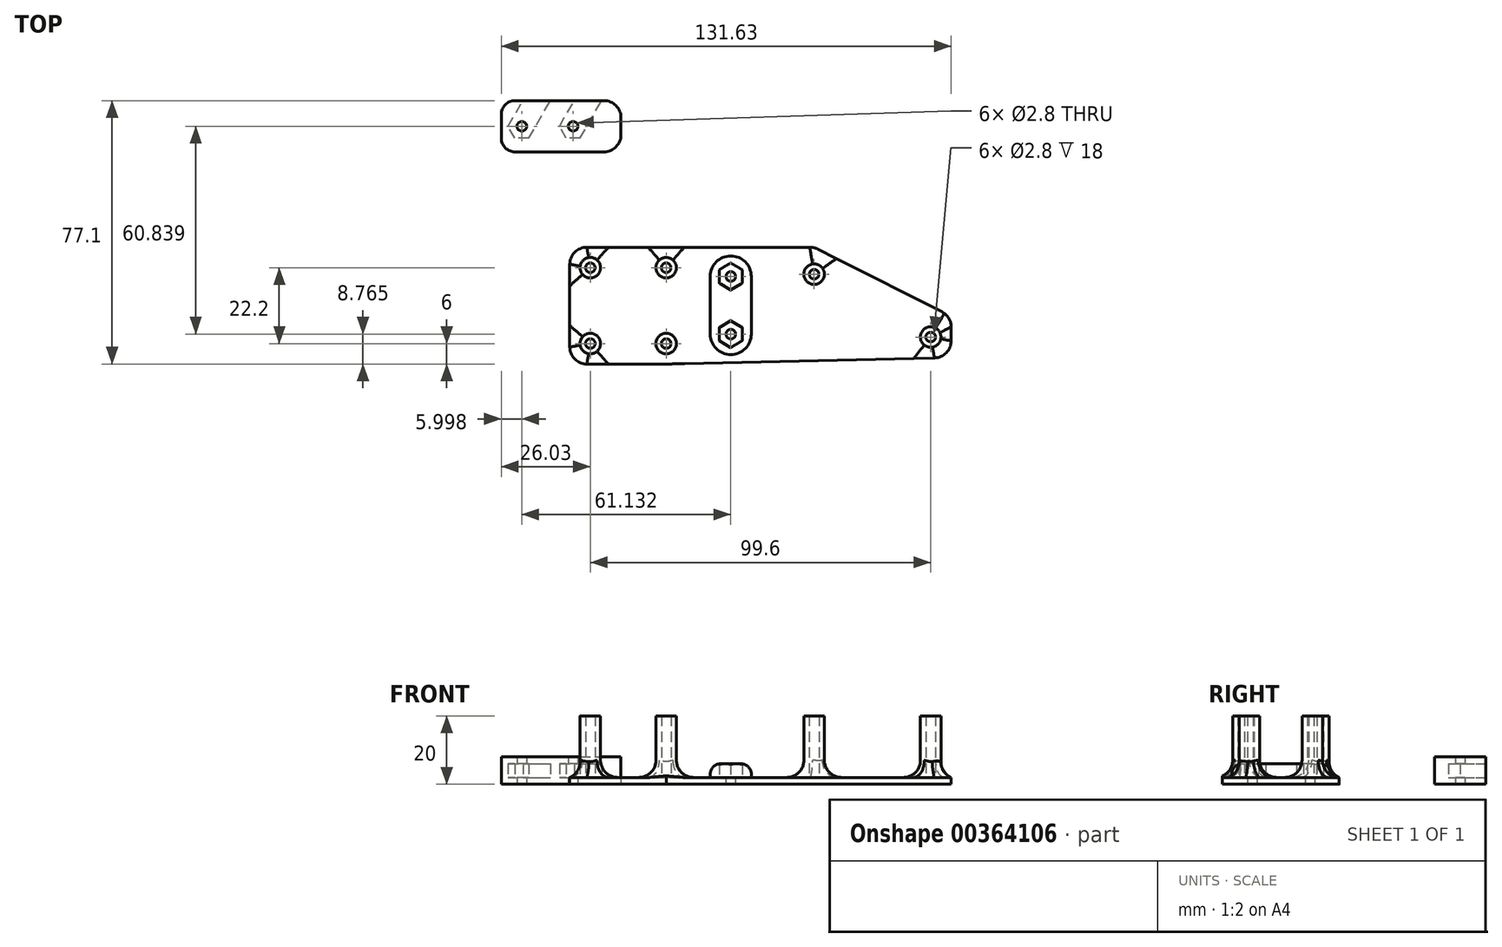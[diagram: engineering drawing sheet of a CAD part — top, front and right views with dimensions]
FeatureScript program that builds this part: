
annotation { "Feature Type Name" : "Feature", "Feature Type Description" : "" }
export const myFeature = defineFeature(function(context is Context, id is Id, definition is map)
    precondition{}
    {
        {
            var Q0;
            Q0=qCreatedBy(makeId("Top.planeOp"),FACE);
            var sketch = newSketch(context, id + "F0", { "sketchPlane" : qUnion([Q0])});
            skLineSegment(sketch, "E0.bottom", {"start": v(-26.1, 11.1) * mm, "end": v(-3.9, 11.1) * mm, "construction": true});
            skLineSegment(sketch, "E0.top", {"start": v(-26.1, -11.1) * mm, "end": v(-3.9, -11.1) * mm, "construction": true});
            skLineSegment(sketch, "E0.left", {"start": v(-26.1, 11.1) * mm, "end": v(-26.1, -11.1) * mm, "construction": true});
            skLineSegment(sketch, "E0.right", {"start": v(-3.9, 11.1) * mm, "end": v(-3.9, -11.1) * mm, "construction": true});
            skCircle(sketch, "E1", {"center": v(-26.1, 11.1) * mm, "radius": 1.4 * mm});
            skCircle(sketch, "E2", {"center": v(-3.9, 11.1) * mm, "radius": 1.4 * mm});
            skCircle(sketch, "E3", {"center": v(-3.9, -11.1) * mm, "radius": 1.4 * mm});
            skCircle(sketch, "E4", {"center": v(-26.1, -11.1) * mm, "radius": 1.4 * mm});
            skCircle(sketch, "E5", {"center": v(-26.1, 11.1) * mm, "radius": 3 * mm});
            skCircle(sketch, "E6", {"center": v(-3.9, 11.1) * mm, "radius": 3 * mm});
            skCircle(sketch, "E7", {"center": v(-3.9, -11.1) * mm, "radius": 3 * mm});
            skCircle(sketch, "E8", {"center": v(-26.1, -11.1) * mm, "radius": 3 * mm});
            skLineSegment(sketch, "E9", {"start": v(-26.1, 11.1) * mm, "end": v(-3.9, -11.1) * mm, "construction": true});
            skLineSegment(sketch, "E10", {"start": v(-26.1, -11.1) * mm, "end": v(-3.9, 11.1) * mm, "construction": true});
            skPoint(sketch, "E11", {"position": v(-15, 0) * mm});
            skLineSegment(sketch, "E12.bottom", {"start": v(-30, 15) * mm, "end": v(0, 15) * mm, "construction": true});
            skLineSegment(sketch, "E12.top", {"start": v(-30, -15) * mm, "end": v(0, -15) * mm, "construction": true});
            skLineSegment(sketch, "E12.left", {"start": v(-30, 15) * mm, "end": v(-30, -15) * mm, "construction": true});
            skLineSegment(sketch, "E12.right", {"start": v(0, 15) * mm, "end": v(0, -15) * mm, "construction": true});
            skLineSegment(sketch, "E13", {"start": v(-15, 15) * mm, "end": v(-15, -15) * mm, "construction": true});
            skLineSegment(sketch, "E14", {"start": v(-30, 0) * mm, "end": v(0, 0) * mm, "construction": true});
            skLineSegment(sketch, "E15.bottom", {"start": v(30, -12) * mm, "end": v(84, -12) * mm, "construction": true});
            skLineSegment(sketch, "E15.top", {"start": v(30, 12) * mm, "end": v(84, 12) * mm, "construction": true});
            skLineSegment(sketch, "E15.left", {"start": v(30, -12) * mm, "end": v(30, 12) * mm, "construction": true});
            skLineSegment(sketch, "E15.right", {"start": v(84, -12) * mm, "end": v(84, 12) * mm, "construction": true});
            skCircle(sketch, "E16", {"center": v(39.4, 9.2) * mm, "radius": 1.4 * mm});
            skCircle(sketch, "E17", {"center": v(73.5, -9.2) * mm, "radius": 1.4 * mm});
            skLineSegment(sketch, "E18", {"start": v(0, 0) * mm, "end": v(15, 0) * mm, "construction": true});
            skCircle(sketch, "E19", {"center": v(39.4, 9.2) * mm, "radius": 3 * mm});
            skCircle(sketch, "E20", {"center": v(73.5, -9.2) * mm, "radius": 3 * mm});
            skLineSegment(sketch, "E21.bottom", {"start": v(-32.1, 17.1) * mm, "end": v(79.5, 17.1) * mm});
            skLineSegment(sketch, "E21.top", {"start": v(-32.1, -17.1) * mm, "end": v(79.5, -17.1) * mm});
            skLineSegment(sketch, "E21.left", {"start": v(-32.1, 17.1) * mm, "end": v(-32.1, -17.1) * mm});
            skLineSegment(sketch, "E21.right", {"start": v(79.5, 17.1) * mm, "end": v(79.5, -3.2) * mm, "construction": true});
            skLineSegment(sketch, "E22", {"start": v(-3.9, -17.1) * mm, "end": v(79.5, -15.2) * mm});
            skLineSegment(sketch, "E23", {"start": v(73.5, -12.2) * mm, "end": v(79.5, -12.2) * mm, "construction": true});
            skLineSegment(sketch, "E24", {"start": v(73.5, -6.2) * mm, "end": v(79.5, -6.2) * mm, "construction": true});
            skLineSegment(sketch, "E25", {"start": v(39.4, 17.1) * mm, "end": v(79.5, -3.2) * mm});
            skLineSegment(sketch, "E26", {"start": v(79.5, -3.2) * mm, "end": v(79.5, -15.2) * mm});
            skLineSegment(sketch, "E27", {"start": v(79.5, -15.2) * mm, "end": v(79.5, -17.1) * mm, "construction": true});
            skLineSegment(sketch, "E28", {"start": v(15, 17.1) * mm, "end": v(15, 0) * mm, "construction": true});
            skPoint(sketch, "E28.startSnap0", {"position": v(15, 0) * mm});
            skLineSegment(sketch, "E29", {"start": v(15, 0) * mm, "end": v(30, 0) * mm, "construction": true});
            skLineSegment(sketch, "E30", {"start": v(15, 0) * mm, "end": v(15, -16.67) * mm, "construction": true});
            skCircle(sketch, "E31.cCircle", {"center": v(15, -8.33) * mm, "radius": 3.9 * mm, "construction": true});
            skLineSegment(sketch, "E31.0", {"start": v(11.62, -6.38) * mm, "end": v(15, -4.43) * mm});
            skLineSegment(sketch, "E31.1", {"start": v(15, -4.43) * mm, "end": v(18.38, -6.38) * mm});
            skLineSegment(sketch, "E31.2", {"start": v(18.38, -6.38) * mm, "end": v(18.38, -10.28) * mm});
            skLineSegment(sketch, "E31.3", {"start": v(18.38, -10.28) * mm, "end": v(15, -12.23) * mm});
            skLineSegment(sketch, "E31.4", {"start": v(15, -12.23) * mm, "end": v(11.62, -10.28) * mm});
            skLineSegment(sketch, "E31.5", {"start": v(11.62, -10.28) * mm, "end": v(11.62, -6.38) * mm});
            skCircle(sketch, "E32.cCircle", {"center": v(15, 8.55) * mm, "radius": 3.9 * mm, "construction": true});
            skLineSegment(sketch, "E32.0", {"start": v(18.38, 6.6) * mm, "end": v(15, 4.65) * mm});
            skLineSegment(sketch, "E32.1", {"start": v(15, 4.65) * mm, "end": v(11.62, 6.6) * mm});
            skLineSegment(sketch, "E32.2", {"start": v(11.62, 6.6) * mm, "end": v(11.62, 10.5) * mm});
            skLineSegment(sketch, "E32.3", {"start": v(11.62, 10.5) * mm, "end": v(15, 12.45) * mm});
            skLineSegment(sketch, "E32.4", {"start": v(15, 12.45) * mm, "end": v(18.38, 10.5) * mm});
            skLineSegment(sketch, "E32.5", {"start": v(18.38, 10.5) * mm, "end": v(18.38, 6.6) * mm});
            skCircle(sketch, "E33", {"center": v(15, -8.33) * mm, "radius": 6 * mm});
            skCircle(sketch, "E34", {"center": v(15, 8.55) * mm, "radius": 6 * mm});
            skLineSegment(sketch, "E35", {"start": v(9, -8.33) * mm, "end": v(9, 8.55) * mm});
            skPoint(sketch, "E35.startSnap0", {"position": v(11.62, -8.33) * mm});
            skLineSegment(sketch, "E36", {"start": v(21, -8.33) * mm, "end": v(21, 8.55) * mm});
            skPoint(sketch, "E36.startSnap0", {"position": v(18.38, -8.33) * mm});
            skCircle(sketch, "E37", {"center": v(15, 8.55) * mm, "radius": 1.4 * mm});
            skCircle(sketch, "E38", {"center": v(15, -8.33) * mm, "radius": 1.4 * mm});
            skSolve(sketch);
        }
        {
            var Q0;
            Q0=makeQuery(id+"F0.imprint","IMPRINT",FACE,{"disambiguationData":[TD([[makeQuery(id+"F0.imprint","IMPRINT",EDGE,{"derivedFrom":sQuery(id+"F0.wireOp",EDGE,"E5")}),-1.0]])]});
            var Q1;
            Q1=makeQuery(id+"F0.imprint","IMPRINT",FACE,{"disambiguationData":[TD([[makeQuery(id+"F0.imprint","IMPRINT",EDGE,{"derivedFrom":sQuery(id+"F0.wireOp",EDGE,"E3")}),-1.0]])]});
            var Q2;
            Q2=makeQuery(id+"F0.imprint","IMPRINT",FACE,{"disambiguationData":[TD([[makeQuery(id+"F0.imprint","IMPRINT",EDGE,{"derivedFrom":sQuery(id+"F0.wireOp",EDGE,"E4")}),-1.0]])]});
            var Q3;
            Q3=makeQuery(id+"F0.imprint","IMPRINT",FACE,{"disambiguationData":[TD([[makeQuery(id+"F0.imprint","IMPRINT",EDGE,{"derivedFrom":sQuery(id+"F0.wireOp",EDGE,"E4")}),1.0]])]});
            var Q4;
            Q4=makeQuery(id+"F0.imprint","IMPRINT",FACE,{"disambiguationData":[TD([[makeQuery(id+"F0.imprint","IMPRINT",EDGE,{"derivedFrom":sQuery(id+"F0.wireOp",EDGE,"E3")}),1.0]])]});
            var Q5;
            Q5=makeQuery(id+"F0.imprint","IMPRINT",FACE,{"disambiguationData":[TD([[makeQuery(id+"F0.imprint","IMPRINT",EDGE,{"derivedFrom":sQuery(id+"F0.wireOp",EDGE,"E2")}),-1.0]])]});
            var Q6;
            Q6=makeQuery(id+"F0.imprint","IMPRINT",FACE,{"disambiguationData":[TD([[makeQuery(id+"F0.imprint","IMPRINT",EDGE,{"derivedFrom":sQuery(id+"F0.wireOp",EDGE,"E2")}),1.0]])]});
            var Q7;
            Q7=makeQuery(id+"F0.imprint","IMPRINT",FACE,{"disambiguationData":[TD([[makeQuery(id+"F0.imprint","IMPRINT",EDGE,{"derivedFrom":sQuery(id+"F0.wireOp",EDGE,"E1")}),1.0]])]});
            var Q8;
            Q8=makeQuery(id+"F0.imprint","IMPRINT",FACE,{"disambiguationData":[TD([[makeQuery(id+"F0.imprint","IMPRINT",EDGE,{"derivedFrom":sQuery(id+"F0.wireOp",EDGE,"E1")}),-1.0]])]});
            var Q9;
            Q9=makeQuery(id+"F0.imprint","IMPRINT",FACE,{"disambiguationData":[TD([[makeQuery(id+"F0.imprint","IMPRINT",EDGE,{"derivedFrom":sQuery(id+"F0.wireOp",EDGE,"E16")}),-1.0]])]});
            var Q10;
            Q10=makeQuery(id+"F0.imprint","IMPRINT",FACE,{"disambiguationData":[TD([[makeQuery(id+"F0.imprint","IMPRINT",EDGE,{"derivedFrom":sQuery(id+"F0.wireOp",EDGE,"E16")}),1.0]])]});
            var Q11;
            {var subQ0=sQuery(id+"F0.wireOp",EDGE,"E35");Q11=makeQuery(id+"F0.imprint","IMPRINT",FACE,{"disambiguationData":[TD([[makeQuery(id+"F0.imprint","IMPRINT",EDGE,{"derivedFrom":subQ0}),-1.0]])]});}
            var Q12;
            Q12=makeQuery(id+"F0.imprint","IMPRINT",FACE,{"disambiguationData":[TD([[makeQuery(id+"F0.imprint","IMPRINT",EDGE,{"derivedFrom":sQuery(id+"F0.wireOp",EDGE,"E32.0")}),1.0]])]});
            var Q13;
            Q13=makeQuery(id+"F0.imprint","IMPRINT",FACE,{"disambiguationData":[TD([[makeQuery(id+"F0.imprint","IMPRINT",EDGE,{"derivedFrom":sQuery(id+"F0.wireOp",EDGE,"E32.0")}),-1.0]])]});
            var Q14;
            Q14=makeQuery(id+"F0.imprint","IMPRINT",FACE,{"disambiguationData":[TD([[makeQuery(id+"F0.imprint","IMPRINT",EDGE,{"derivedFrom":sQuery(id+"F0.wireOp",EDGE,"E31.0")}),-1.0]])]});
            var Q15;
            Q15=makeQuery(id+"F0.imprint","IMPRINT",FACE,{"disambiguationData":[TD([[makeQuery(id+"F0.imprint","IMPRINT",EDGE,{"derivedFrom":sQuery(id+"F0.wireOp",EDGE,"E31.0")}),1.0]])]});
            var Q16;
            Q16=makeQuery(id+"F0.imprint","IMPRINT",FACE,{"disambiguationData":[TD([[makeQuery(id+"F0.imprint","IMPRINT",EDGE,{"derivedFrom":sQuery(id+"F0.wireOp",EDGE,"E17")}),-1.0]])]});
            var Q17;
            Q17=makeQuery(id+"F0.imprint","IMPRINT",FACE,{"disambiguationData":[TD([[makeQuery(id+"F0.imprint","IMPRINT",EDGE,{"derivedFrom":sQuery(id+"F0.wireOp",EDGE,"E17")}),1.0]])]});
            extrude(context, id + "F1", {"entities" : qUnion([Q0, Q1, Q2, Q3, Q4, Q5, Q6, Q7, Q8, Q9, Q10, Q11, Q12, Q13, Q14, Q15, Q16, Q17]), "depth" : 2 * mm});
        }
        {
            var Q0;
            Q0=makeQuery(id+"F0.imprint","IMPRINT",FACE,{"disambiguationData":[TD([[makeQuery(id+"F0.imprint","IMPRINT",EDGE,{"derivedFrom":sQuery(id+"F0.wireOp",EDGE,"E4")}),-1.0]])]});
            var Q1;
            Q1=makeQuery(id+"F0.imprint","IMPRINT",FACE,{"disambiguationData":[TD([[makeQuery(id+"F0.imprint","IMPRINT",EDGE,{"derivedFrom":sQuery(id+"F0.wireOp",EDGE,"E3")}),-1.0]])]});
            var Q2;
            Q2=makeQuery(id+"F0.imprint","IMPRINT",FACE,{"disambiguationData":[TD([[makeQuery(id+"F0.imprint","IMPRINT",EDGE,{"derivedFrom":sQuery(id+"F0.wireOp",EDGE,"E2")}),-1.0]])]});
            var Q3;
            Q3=makeQuery(id+"F0.imprint","IMPRINT",FACE,{"disambiguationData":[TD([[makeQuery(id+"F0.imprint","IMPRINT",EDGE,{"derivedFrom":sQuery(id+"F0.wireOp",EDGE,"E1")}),-1.0]])]});
            var Q4;
            Q4=makeQuery(id+"F0.imprint","IMPRINT",FACE,{"disambiguationData":[TD([[makeQuery(id+"F0.imprint","IMPRINT",EDGE,{"derivedFrom":sQuery(id+"F0.wireOp",EDGE,"E16")}),-1.0]])]});
            var Q5;
            Q5=makeQuery(id+"F0.imprint","IMPRINT",FACE,{"disambiguationData":[TD([[makeQuery(id+"F0.imprint","IMPRINT",EDGE,{"derivedFrom":sQuery(id+"F0.wireOp",EDGE,"E17")}),-1.0]])]});
            extrude(context, id + "F2", {"entities" : qUnion([Q0, Q1, Q2, Q3, Q4, Q5]), "operationType" : NewBodyOperationType.ADD, "depth" : 20 * mm});
        }
        {
            var Q0;
            Q0=makeQuery(id+"F0.imprint","IMPRINT",FACE,{"disambiguationData":[TD([[makeQuery(id+"F0.imprint","IMPRINT",EDGE,{"derivedFrom":sQuery(id+"F0.wireOp",EDGE,"E31.0")}),1.0]])]});
            var Q1;
            Q1=makeQuery(id+"F0.imprint","IMPRINT",FACE,{"disambiguationData":[TD([[makeQuery(id+"F0.imprint","IMPRINT",EDGE,{"derivedFrom":sQuery(id+"F0.wireOp",EDGE,"E32.0")}),1.0]])]});
            var Q2;
            {var subQ0=sQuery(id+"F0.wireOp",EDGE,"E35");Q2=makeQuery(id+"F0.imprint","IMPRINT",FACE,{"disambiguationData":[TD([[makeQuery(id+"F0.imprint","IMPRINT",EDGE,{"derivedFrom":subQ0}),-1.0]])]});}
            extrude(context, id + "F3", {"entities" : qUnion([Q0, Q1, Q2]), "operationType" : NewBodyOperationType.ADD, "depth" : 6 * mm});
        }
        {
            var Q0;
            Q0=makeQuery(id+"F1.opExtrude","SWEPT_EDGE",EDGE,{"disambiguationData":[OSD([sQuery(id+"F0.wireOp",EDGE,"E21.top"),sQuery(id+"F0.wireOp",EDGE,"E21.left")])]});
            var Q1;
            Q1=makeQuery(id+"F1.opExtrude","SWEPT_EDGE",EDGE,{"disambiguationData":[OSD([sQuery(id+"F0.wireOp",EDGE,"E21.bottom"),sQuery(id+"F0.wireOp",EDGE,"E21.left")])]});
            var Q2;
            Q2=makeQuery(id+"F1.opExtrude","SWEPT_EDGE",EDGE,{"disambiguationData":[OSD([sQuery(id+"F0.wireOp",EDGE,"E21.bottom"),sQuery(id+"F0.wireOp",EDGE,"E25")])]});
            var Q3;
            Q3=makeQuery(id+"F1.opExtrude","SWEPT_EDGE",EDGE,{"disambiguationData":[OSD([sQuery(id+"F0.wireOp",EDGE,"E25"),sQuery(id+"F0.wireOp",EDGE,"E26")])]});
            var Q4;
            Q4=makeQuery(id+"F1.opExtrude","SWEPT_EDGE",EDGE,{"disambiguationData":[OSD([sQuery(id+"F0.wireOp",EDGE,"E22"),sQuery(id+"F0.wireOp",EDGE,"E26")])]});
            fillet(context, id + "F4", {"entities" : qUnion([Q0, Q1, Q2, Q3, Q4]), "radius" : 5 * mm, "tangentPropagation" : true, "allowEdgeOverflow" : false});
        }
        {
            var Q0;
            Q0=makeQuery(id+"F2.boolean.opBoolean","INTERSECT",EDGE,{"derivedFrom":[makeQuery(id+"F1.opExtrude","CAP_FACE",FACE,{"disambiguationData":[OSD([sQuery(id+"F0.wireOp",EDGE,"E21.bottom"),sQuery(id+"F0.wireOp",EDGE,"E21.top"),sQuery(id+"F0.wireOp",EDGE,"E21.left"),sQuery(id+"F0.wireOp",EDGE,"E22"),sQuery(id+"F0.wireOp",EDGE,"E25"),sQuery(id+"F0.wireOp",EDGE,"E26"),sQuery(id+"F0.wireOp",EDGE,"E37"),sQuery(id+"F0.wireOp",EDGE,"E38")])],"isStart":false}),makeQuery(id+"F2.opExtrude","SWEPT_FACE",FACE,{"disambiguationData":[OSD([sQuery(id+"F0.wireOp",EDGE,"E5")])]})]});
            var Q1;
            Q1=makeQuery(id+"F2.boolean.opBoolean","INTERSECT",EDGE,{"derivedFrom":[makeQuery(id+"F1.opExtrude","CAP_FACE",FACE,{"disambiguationData":[OSD([sQuery(id+"F0.wireOp",EDGE,"E21.bottom"),sQuery(id+"F0.wireOp",EDGE,"E21.top"),sQuery(id+"F0.wireOp",EDGE,"E21.left"),sQuery(id+"F0.wireOp",EDGE,"E22"),sQuery(id+"F0.wireOp",EDGE,"E25"),sQuery(id+"F0.wireOp",EDGE,"E26"),sQuery(id+"F0.wireOp",EDGE,"E37"),sQuery(id+"F0.wireOp",EDGE,"E38")])],"isStart":false}),makeQuery(id+"F2.opExtrude","SWEPT_FACE",FACE,{"disambiguationData":[OSD([sQuery(id+"F0.wireOp",EDGE,"E6")])]})]});
            var Q2;
            Q2=makeQuery(id+"F2.boolean.opBoolean","INTERSECT",EDGE,{"derivedFrom":[makeQuery(id+"F1.opExtrude","CAP_FACE",FACE,{"disambiguationData":[OSD([sQuery(id+"F0.wireOp",EDGE,"E21.bottom"),sQuery(id+"F0.wireOp",EDGE,"E21.top"),sQuery(id+"F0.wireOp",EDGE,"E21.left"),sQuery(id+"F0.wireOp",EDGE,"E22"),sQuery(id+"F0.wireOp",EDGE,"E25"),sQuery(id+"F0.wireOp",EDGE,"E26"),sQuery(id+"F0.wireOp",EDGE,"E37"),sQuery(id+"F0.wireOp",EDGE,"E38")])],"isStart":false}),makeQuery(id+"F2.opExtrude","SWEPT_FACE",FACE,{"disambiguationData":[OSD([sQuery(id+"F0.wireOp",EDGE,"E8")])]})]});
            var Q3;
            Q3=makeQuery(id+"F2.boolean.opBoolean","INTERSECT",EDGE,{"derivedFrom":[makeQuery(id+"F1.opExtrude","CAP_FACE",FACE,{"disambiguationData":[OSD([sQuery(id+"F0.wireOp",EDGE,"E21.bottom"),sQuery(id+"F0.wireOp",EDGE,"E21.top"),sQuery(id+"F0.wireOp",EDGE,"E21.left"),sQuery(id+"F0.wireOp",EDGE,"E22"),sQuery(id+"F0.wireOp",EDGE,"E25"),sQuery(id+"F0.wireOp",EDGE,"E26"),sQuery(id+"F0.wireOp",EDGE,"E37"),sQuery(id+"F0.wireOp",EDGE,"E38")])],"isStart":false}),makeQuery(id+"F2.opExtrude","SWEPT_FACE",FACE,{"disambiguationData":[OSD([sQuery(id+"F0.wireOp",EDGE,"E7")])]})]});
            var Q4;
            Q4=makeQuery(id+"F2.boolean.opBoolean","INTERSECT",EDGE,{"derivedFrom":[makeQuery(id+"F1.opExtrude","CAP_FACE",FACE,{"disambiguationData":[OSD([sQuery(id+"F0.wireOp",EDGE,"E21.bottom"),sQuery(id+"F0.wireOp",EDGE,"E21.top"),sQuery(id+"F0.wireOp",EDGE,"E21.left"),sQuery(id+"F0.wireOp",EDGE,"E22"),sQuery(id+"F0.wireOp",EDGE,"E25"),sQuery(id+"F0.wireOp",EDGE,"E26"),sQuery(id+"F0.wireOp",EDGE,"E37"),sQuery(id+"F0.wireOp",EDGE,"E38")])],"isStart":false}),makeQuery(id+"F2.opExtrude","SWEPT_FACE",FACE,{"disambiguationData":[OSD([sQuery(id+"F0.wireOp",EDGE,"E19")])]})]});
            var Q5;
            Q5=makeQuery(id+"F2.boolean.opBoolean","INTERSECT",EDGE,{"derivedFrom":[makeQuery(id+"F1.opExtrude","CAP_FACE",FACE,{"disambiguationData":[OSD([sQuery(id+"F0.wireOp",EDGE,"E21.bottom"),sQuery(id+"F0.wireOp",EDGE,"E21.top"),sQuery(id+"F0.wireOp",EDGE,"E21.left"),sQuery(id+"F0.wireOp",EDGE,"E22"),sQuery(id+"F0.wireOp",EDGE,"E25"),sQuery(id+"F0.wireOp",EDGE,"E26"),sQuery(id+"F0.wireOp",EDGE,"E37"),sQuery(id+"F0.wireOp",EDGE,"E38")])],"isStart":false}),makeQuery(id+"F2.opExtrude","SWEPT_FACE",FACE,{"disambiguationData":[OSD([sQuery(id+"F0.wireOp",EDGE,"E20")])]})]});
            fillet(context, id + "F5", {"entities" : qUnion([Q0, Q1, Q2, Q3, Q4, Q5]), "radius" : 5 * mm, "tangentPropagation" : true, "allowEdgeOverflow" : false});
        }
        {
            var Q0;
            Q0=makeQuery(id+"F3.opExtrude","CAP_EDGE",EDGE,{"disambiguationData":[OSD([sQuery(id+"F0.wireOp",EDGE,"E33")])],"isStart":false});
            fillet(context, id + "F6", {"entities" : qUnion([Q0]), "radius" : 3 * mm, "tangentPropagation" : true, "allowEdgeOverflow" : false});
        }
        {
            var Q0;
            Q0=qCreatedBy(makeId("Top.planeOp"),FACE);
            var sketch = newSketch(context, id + "F7", { "sketchPlane" : qUnion([Q0])});
            skLineSegment(sketch, "E39.bottom", {"start": v(-48.13, 60) * mm, "end": v(-45.8, 60) * mm});
            skLineSegment(sketch, "E39.top", {"start": v(-48.13, 45) * mm, "end": v(-22.13, 45) * mm});
            skLineSegment(sketch, "E39.left", {"start": v(-52.13, 56) * mm, "end": v(-52.13, 49) * mm});
            skLineSegment(sketch, "E39.right", {"start": v(-17.13, 55) * mm, "end": v(-17.13, 50) * mm});
            skCircle(sketch, "E40", {"center": v(-31.13, 52.5) * mm, "radius": 1.4 * mm});
            skCircle(sketch, "E41", {"center": v(-46.13, 52.5) * mm, "radius": 1.4 * mm});
            skLineSegment(sketch, "E42", {"start": v(-17.13, 52.5) * mm, "end": v(-52.13, 52.5) * mm, "construction": true});
            skCircle(sketch, "E43.cCircle", {"center": v(-31.13, 52.5) * mm, "radius": 4 * mm, "construction": true});
            skLineSegment(sketch, "E43.0", {"start": v(-27.13, 52.5) * mm, "end": v(-29.13, 49.04) * mm});
            skLineSegment(sketch, "E43.1", {"start": v(-29.13, 49.04) * mm, "end": v(-33.13, 49.04) * mm});
            skLineSegment(sketch, "E43.2", {"start": v(-33.13, 49.04) * mm, "end": v(-35.13, 52.5) * mm});
            skLineSegment(sketch, "E43.3", {"start": v(-35.13, 52.5) * mm, "end": v(-33.13, 55.97) * mm});
            skLineSegment(sketch, "E43.4", {"start": v(-33.13, 55.97) * mm, "end": v(-29.13, 55.97) * mm});
            skLineSegment(sketch, "E43.5", {"start": v(-29.13, 55.97) * mm, "end": v(-27.13, 52.5) * mm});
            skCircle(sketch, "E44.cCircle", {"center": v(-46.13, 52.5) * mm, "radius": 4 * mm, "construction": true});
            skLineSegment(sketch, "E44.0", {"start": v(-42.13, 52.5) * mm, "end": v(-44.13, 49.04) * mm});
            skLineSegment(sketch, "E44.1", {"start": v(-44.13, 49.04) * mm, "end": v(-48.13, 49.04) * mm});
            skLineSegment(sketch, "E44.2", {"start": v(-48.13, 49.04) * mm, "end": v(-50.13, 52.5) * mm});
            skLineSegment(sketch, "E44.3", {"start": v(-50.13, 52.5) * mm, "end": v(-48.13, 55.97) * mm});
            skLineSegment(sketch, "E44.4", {"start": v(-48.13, 55.97) * mm, "end": v(-44.13, 55.97) * mm});
            skLineSegment(sketch, "E44.5", {"start": v(-44.13, 55.97) * mm, "end": v(-42.13, 52.5) * mm});
            skLineSegment(sketch, "E45", {"start": v(-33.13, 55.97) * mm, "end": v(-30.8, 60) * mm});
            skLineSegment(sketch, "E46", {"start": v(-27.13, 52.5) * mm, "end": v(-22.8, 60) * mm});
            skLineSegment(sketch, "E47", {"start": v(-42.13, 52.5) * mm, "end": v(-37.8, 60) * mm});
            skLineSegment(sketch, "E48", {"start": v(-22.8, 60) * mm, "end": v(-22.13, 60) * mm});
            skLineSegment(sketch, "E49", {"start": v(-30.8, 60) * mm, "end": v(-22.8, 60) * mm});
            skLineSegment(sketch, "E50", {"start": v(-37.8, 60) * mm, "end": v(-30.8, 60) * mm});
            skLineSegment(sketch, "E51", {"start": v(-45.8, 60) * mm, "end": v(-37.8, 60) * mm});
            skPoint(sketch, "E52.visualSharp", {"position": v(-17.13, 60) * mm});
            skArc(sketch, "E52.filletArc", {"start": v(-17.13, 55) * mm, "mid": v(-18.6, 58.54) * mm, "end": v(-22.13, 60) * mm});
            skPoint(sketch, "E53.visualSharp", {"position": v(-17.13, 45) * mm});
            skArc(sketch, "E53.filletArc", {"start": v(-22.13, 45) * mm, "mid": v(-18.6, 46.47) * mm, "end": v(-17.13, 50) * mm});
            skPoint(sketch, "E54.visualSharp", {"position": v(-52.13, 45) * mm});
            skArc(sketch, "E54.filletArc", {"start": v(-52.13, 49) * mm, "mid": v(-50.96, 46.18) * mm, "end": v(-48.13, 45) * mm});
            skLineSegment(sketch, "E55", {"start": v(-48.13, 55.97) * mm, "end": v(-45.8, 60) * mm});
            skPoint(sketch, "E56.visualSharp", {"position": v(-52.13, 60) * mm});
            skArc(sketch, "E56.filletArc", {"start": v(-48.13, 60) * mm, "mid": v(-50.96, 58.83) * mm, "end": v(-52.13, 56) * mm});
            skSolve(sketch);
        }
        {
            var Q0;
            Q0=makeQuery(id+"F7.imprint","IMPRINT",FACE,{"disambiguationData":[TD([[makeQuery(id+"F7.imprint","IMPRINT",EDGE,{"derivedFrom":sQuery(id+"F7.wireOp",EDGE,"E39.bottom")}),-1.0]])]});
            var Q1;
            Q1=makeQuery(id+"F7.imprint","IMPRINT",FACE,{"disambiguationData":[TD([[makeQuery(id+"F7.imprint","IMPRINT",EDGE,{"derivedFrom":sQuery(id+"F7.wireOp",EDGE,"E41")}),-1.0]])]});
            var Q2;
            Q2=makeQuery(id+"F7.imprint","IMPRINT",FACE,{"disambiguationData":[TD([[makeQuery(id+"F7.imprint","IMPRINT",EDGE,{"derivedFrom":sQuery(id+"F7.wireOp",EDGE,"E44.4")}),1.0]])]});
            var Q3;
            Q3=makeQuery(id+"F7.imprint","IMPRINT",FACE,{"disambiguationData":[TD([[makeQuery(id+"F7.imprint","IMPRINT",EDGE,{"derivedFrom":sQuery(id+"F7.wireOp",EDGE,"E40")}),-1.0]])]});
            var Q4;
            Q4=makeQuery(id+"F7.imprint","IMPRINT",FACE,{"disambiguationData":[TD([[makeQuery(id+"F7.imprint","IMPRINT",EDGE,{"derivedFrom":sQuery(id+"F7.wireOp",EDGE,"E43.4")}),1.0]])]});
            extrude(context, id + "F8", {"entities" : qUnion([Q0, Q1, Q2, Q3, Q4]), "depth" : 8 * mm});
        }
        {
            var Q0;
            Q0=makeQuery(id+"F7.imprint","IMPRINT",FACE,{"disambiguationData":[TD([[makeQuery(id+"F7.imprint","IMPRINT",EDGE,{"derivedFrom":sQuery(id+"F7.wireOp",EDGE,"E44.4")}),1.0]])]});
            var Q1;
            Q1=makeQuery(id+"F7.imprint","IMPRINT",FACE,{"disambiguationData":[TD([[makeQuery(id+"F7.imprint","IMPRINT",EDGE,{"derivedFrom":sQuery(id+"F7.wireOp",EDGE,"E41")}),-1.0]])]});
            var Q2;
            Q2=makeQuery(id+"F7.imprint","IMPRINT",FACE,{"disambiguationData":[TD([[makeQuery(id+"F7.imprint","IMPRINT",EDGE,{"derivedFrom":sQuery(id+"F7.wireOp",EDGE,"E43.4")}),1.0]])]});
            var Q3;
            Q3=makeQuery(id+"F7.imprint","IMPRINT",FACE,{"disambiguationData":[TD([[makeQuery(id+"F7.imprint","IMPRINT",EDGE,{"derivedFrom":sQuery(id+"F7.wireOp",EDGE,"E40")}),-1.0]])]});
            extrude(context, id + "F9", {"entities" : qUnion([Q0, Q1, Q2, Q3]), "operationType" : NewBodyOperationType.REMOVE, "depth" : 6 * mm, "hasSecondDirection" : true, "secondDirectionOppositeDirection" : false, "secondDirectionDepth" : 2 * mm});
        }
    });
